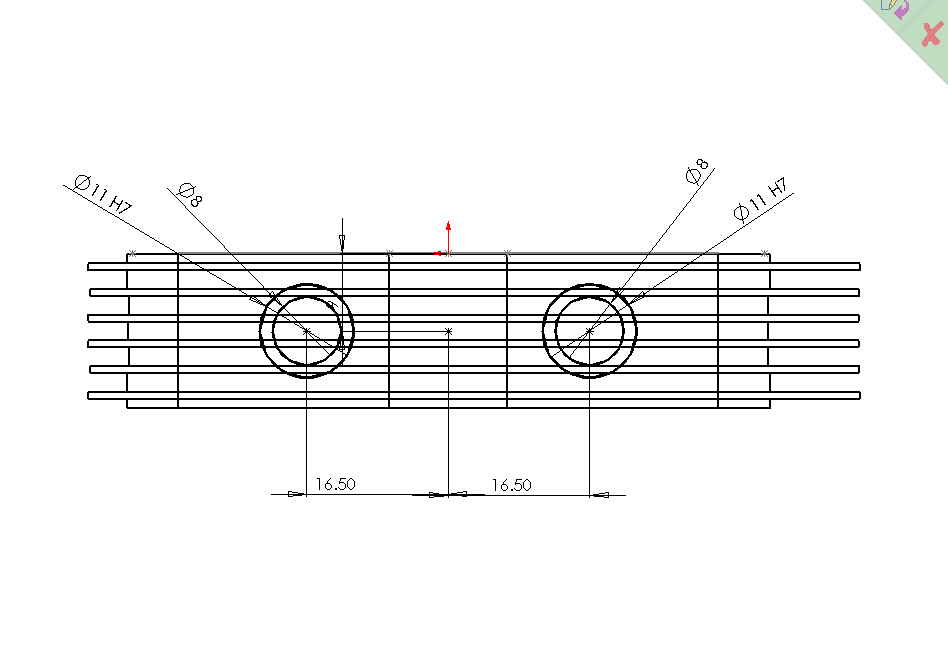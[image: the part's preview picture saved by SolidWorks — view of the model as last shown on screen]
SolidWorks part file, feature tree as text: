
SOLIDWORKS PART (.sldprt)
format: sldprt  version: not decoded by parser v0  size: 338,432 bytes
history: native  units: mm
features: sketch x5, cut_extrude x3, plane x1 + 6 further entries (+8 scaffold rows collapsed)
feature tree (23):
  scaffold x8  (default folders/planes/origin — collapsed)
  "1.zylinder_fin<3>@1.zylinder_combined-"
  "1.zylinder_fin<1>@1.zylinder_combined-"
  "1.zylinder_fin<2>@1.zylinder_combined-"
  "1.zylinder_fin<5>@1.zylinder_combined-"
  "1.zylinder_fin<6>@1.zylinder_combined-"
  "1.zylinder_base<1>@1.zylinder_combined-"
  sketch  "Sketch2"  dims[c1.D2=49.2mm c1.D4=49.2mm c1.D1=6.9mm c1.D3=6.9mm c1.D5=13.8mm c1.D6=13.8mm c2.D5=6.9mm c2.D6=6.9mm c2.D7=31.0mm c2.D8=31.0mm c2.D9=30.0mm c2.D10=30.0mm]
  sketch  "Sketch3"
  cut_extrude  "Cut-Extrude2"  Depth=18mm
  plane  "Plane1"  Offset=1.5mm
  sketch  "Sketch5"  dims[D4=8.0mm D5=8.0mm D6=11.0mm D7=11.0mm D1=9.0mm D2=16.5mm D3=16.5mm]
  sketch  "Sketch7"
  sketch  "Sketch6"
  cut_extrude  "Cut-Extrude3"  Depth=10mm
  cut_extrude  "Cut-Extrude4"  Depth=50mm
decode coverage: 5 of 8 modeling features carry decoded parameters; 6 rows unclassified (native names shown)
note: suppression state not decoded; provenance and decode notes live in map.json
